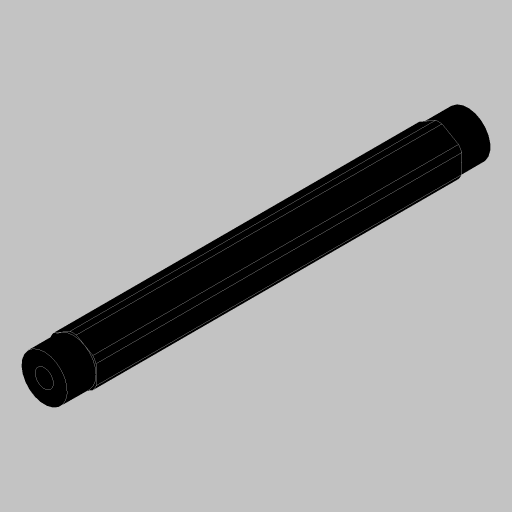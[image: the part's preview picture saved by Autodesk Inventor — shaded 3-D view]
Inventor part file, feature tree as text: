
AUTODESK INVENTOR PART (.ipt)
format: ipt  version: 2023.5 (Build 275446000, 446)  size: 161,792 bytes
history: native  units: in
note: dims shown in document units (in); Inventor stores cm internally (conversion verified against a paired STEP export)
features: extrude x3, projected_geometry x3, hole x1, mirror x1, sketch x1
ambient origin geometry x8: Origin, YZ Plane, XZ Plane, XY Plane, X Axis, Y Axis, Z Axis, Center Point
bodies: Solid1 (feature_tree)
feature tree (9):
  extrude  "Extrusion1"  Depth=0.315in
  hole  "Hole1"  [1 undecoded]
  extrude  "Extrusion3"  Depth=0.5in
  extrude  "Extrusion4"  Depth=0.315in TaperAngle=0.0deg
  mirror  "Mirror2"
  sketch  "Sketch5"  dims[d2=0.0in d9=0.625in d10=0.385in d11=0.25in d12=0.5635in d13=1.0in d14=0.8108in d16=0.7in d17=0.0in d18=0.0in d19=0.5in d20=0.315in d21=0.0in]
  projected_geometry  "Project Cut Edges1"
  projected_geometry  "Project Cut Edges2"
  projected_geometry  "Project Cut Edges3"
note: 1 required parameter value undecoded (feature->parameter linkage not recoverable at this tier; creation-order binding heuristic only, values carry confidence <= 0.55)
